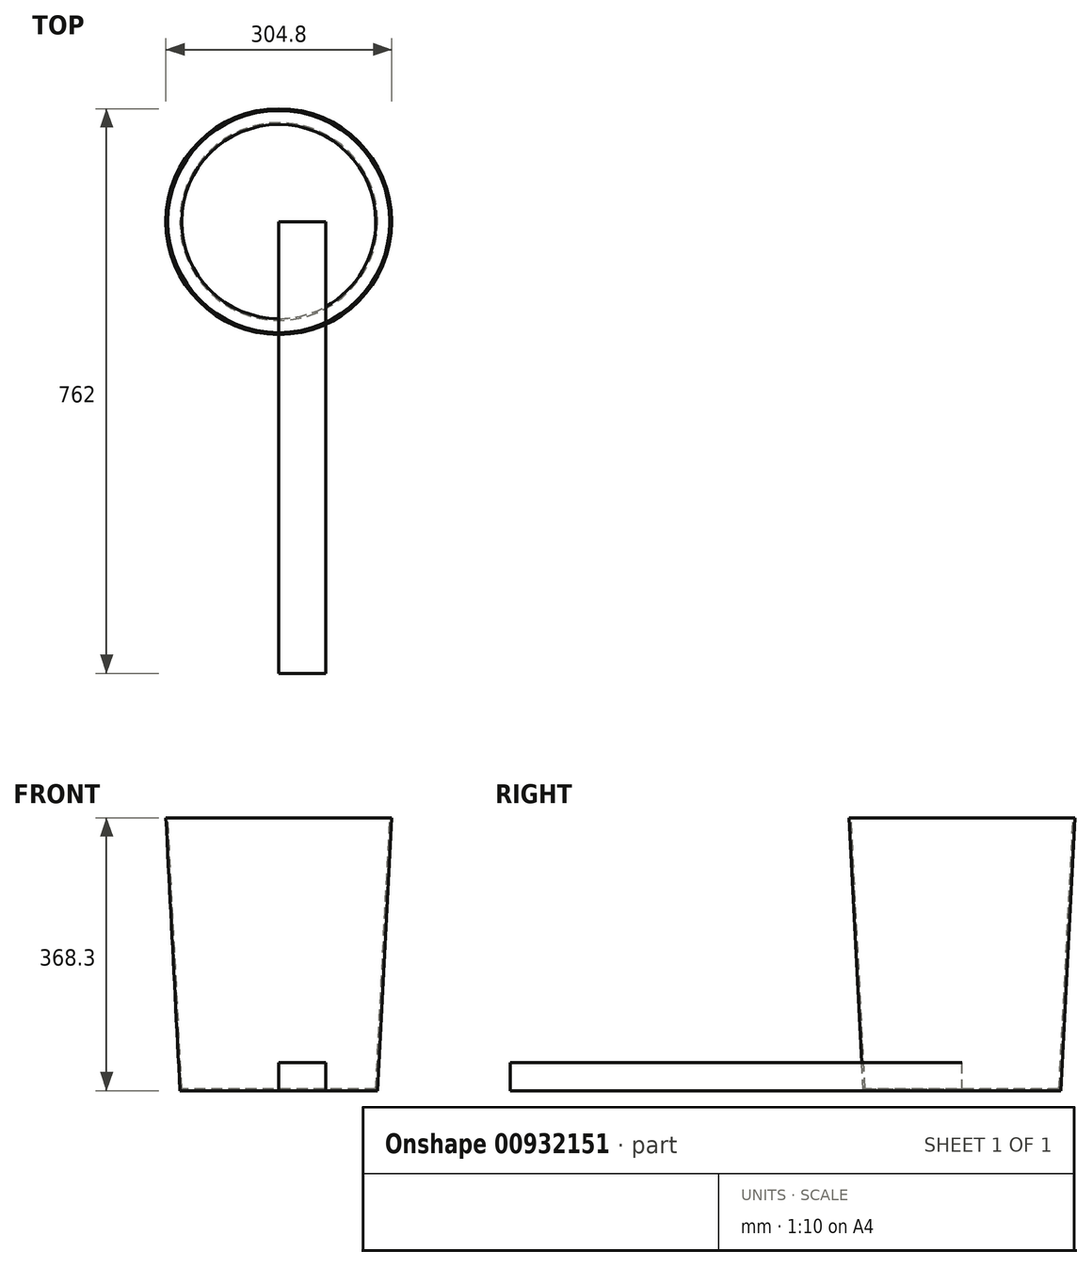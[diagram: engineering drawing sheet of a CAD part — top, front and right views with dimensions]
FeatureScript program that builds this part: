
annotation { "Feature Type Name" : "Feature", "Feature Type Description" : "" }
export const myFeature = defineFeature(function(context is Context, id is Id, definition is map)
    precondition{}
    {
        {
            var Q0;
            Q0=qCreatedBy(makeId("Front.planeOp"),FACE);
            var sketch = newSketch(context, id + "F0", { "sketchPlane" : qUnion([Q0])});
            skLineSegment(sketch, "E0", {"start": v(0, 0) * mm, "end": v(0, 368.3) * mm});
            skLineSegment(sketch, "E1", {"start": v(0, 368.3) * mm, "end": v(-152.4, 368.3) * mm});
            skLineSegment(sketch, "E2", {"start": v(-152.4, 368.3) * mm, "end": v(-133.35, 0) * mm});
            skLineSegment(sketch, "E3", {"start": v(-133.35, 0) * mm, "end": v(0, 0) * mm});
            skSolve(sketch);
        }
        {
            var Q0;
            Q0=makeQuery(id+"F0.imprint","IMPRINT",FACE,{"disambiguationData":[TD([[makeQuery(id+"F0.imprint","IMPRINT",EDGE,{"derivedFrom":sQuery(id+"F0.wireOp",EDGE,"E0")}),1.0]])]});
            var Q1;
            Q1=sQuery(id+"F0.wireOp",EDGE,"E0");
            revolve(context, id + "F1", {"surfaceOperationType" : NewSurfaceOperationType.NEW, "entities" : qUnion([Q0]), "axis" : qUnion([Q1]), "revolveType" : RevolveType.FULL});
        }
        {
            var Q0;
            Q0=makeQuery(id+"F1.opRevolve","SWEPT_FACE",FACE,{"disambiguationData":[OSD([sQuery(id+"F0.wireOp",EDGE,"E1")])]});
            shell(context, id + "F2", {"entities" : qUnion([Q0]), "thickness" : 2.54 * mm});
        }
        {
            var Q0;
            Q0=qCreatedBy(makeId("Front.planeOp"),FACE);
            var sketch = newSketch(context, id + "F3", { "sketchPlane" : qUnion([Q0])});
            skLineSegment(sketch, "E4.bottom", {"start": v(0, 0) * mm, "end": v(63.5, 0) * mm});
            skLineSegment(sketch, "E4.top", {"start": v(0, 38.1) * mm, "end": v(63.5, 38.1) * mm});
            skLineSegment(sketch, "E4.left", {"start": v(0, 0) * mm, "end": v(0, 38.1) * mm});
            skLineSegment(sketch, "E4.right", {"start": v(63.5, 0) * mm, "end": v(63.5, 38.1) * mm});
            skSolve(sketch);
        }
        {
            var Q0;
            Q0 = qSketchRegion(id + "F3", true);
            extrude(context, id + "F4", {"entities" : qUnion([Q0]), "depth" : 609.6 * mm, "offsetDistance" : 25.4 * mm});
        }
    });
